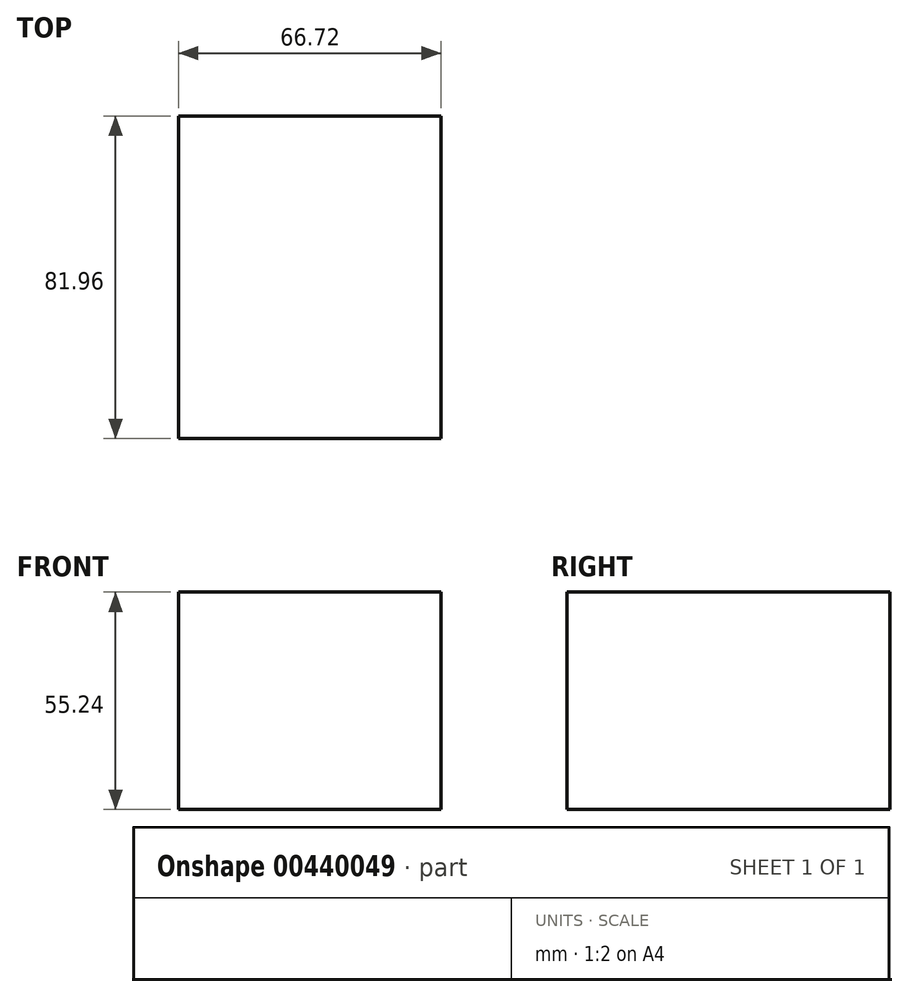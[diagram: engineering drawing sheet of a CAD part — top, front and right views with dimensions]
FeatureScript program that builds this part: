
annotation { "Feature Type Name" : "Feature", "Feature Type Description" : "" }
export const myFeature = defineFeature(function(context is Context, id is Id, definition is map)
    precondition{}
    {
        {
            var Q0;
            Q0=qCreatedBy(makeId("Front.planeOp"),FACE);
            var sketch = newSketch(context, id + "F0", { "sketchPlane" : qUnion([Q0])});
            skLineSegment(sketch, "E0.bottom", {"start": v(-38.95, 45.31) * mm, "end": v(27.77, 45.31) * mm});
            skLineSegment(sketch, "E0.top", {"start": v(-38.95, -9.93) * mm, "end": v(27.77, -9.93) * mm});
            skLineSegment(sketch, "E0.left", {"start": v(-38.95, 45.31) * mm, "end": v(-38.95, -9.93) * mm});
            skLineSegment(sketch, "E0.right", {"start": v(27.77, 45.31) * mm, "end": v(27.77, -9.93) * mm});
            skSolve(sketch);
        }
        {
            var Q0;
            Q0 = qSketchRegion(id + "F0", true);
            extrude(context, id + "F1", {"entities" : qUnion([Q0]), "depth" : 56.56 * mm, "hasSecondDirection" : true, "secondDirectionOppositeDirection" : true, "secondDirectionDepth" : 25.4 * mm});
        }
    });
